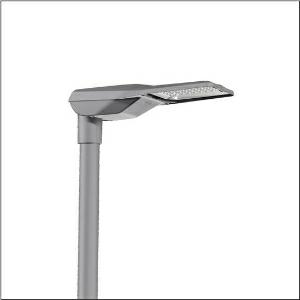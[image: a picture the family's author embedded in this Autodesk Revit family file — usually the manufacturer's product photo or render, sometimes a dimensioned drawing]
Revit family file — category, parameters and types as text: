
# Revit family: streetlight_sl_21_iq_mini___st0_5a_5xe2b41d08gb_120c
name_source: partatom
category: Lighting Fixtures
units: mm (PartAtom-declared; Revit-internal decimal feet)

## family parameters
Cut with Voids When Loaded = No
Host = Face
Light Source = No
Part Type = Normal
Room Calculation Point = No
Round Connector Dimension = Use Diameter
Shared = No

## types (1)
- --- (1 x LED, 5920 lm, 37.1 W, 4000K)
    Apparent Load = 37 VA
    CIE Flux Codes = 41 75 97 100 100
    Color Rendering = 70
    Color Temperature = 4000K
    Default Elevation = 1800 mm
    Description = Streetlight SL 21 iQ mini, mast luminaire, primary light control with lens, of PMMA, primary optical cover: cover, of toughened safety glass, transparent, light distribution: ST0.5a, light emission: direct distribution, primary light characteristic: asymmetric, installation type: post-top, side-entry, LED, High Power LED, rated luminous flux: 5.920lm, luminous efficacy: 160lm/W, light colour: 740, colour temperature: 4000K, control gear: iQ-Comfort, control: Auto-Match, Temp-Guard, Lumen-Switch, Night-Set, Smart-Wire, Light-Fading, Desk-Remote (wireless, voltage-free reading and setting of iQ features in the workshop via application-optimized NFC function/RFID function), optimised constant luminous flux control (CLO 2.0), pre-setting: linear dimming characteristic, mains connection: 220..240V, AC, 50/60Hz, start of lifetime: 37W, end of service life: 39W, reduction: 18W, luminaire housing, of diecast aluminium, powder-coated, SITECO metallic grey (DB 702S), corrosivity category C5 high according to DIN EN ISO 12944, please order mast flange separately, inclination adjustable: 0°, 5°, 10°, 15°, sealing non-destructively replaceable, multi-level sealing system, length: 628mm, width: 235mm, height: 110mm, mast flange for spigot size: 42mm (side-entry): 5XC10008XM4, 60/48mm (side-entry/post-top): 5XC10108XM2, 76/60mm (side-entry/post-top): 5XC10108XM1, mounting height: 4..8m, protection rating (complete): IP66, insulation class (complete): insulation class II (safety insulation), certification: CE, ENEC, ENEC+, VDE, impact resistance: IK10, permissible operating ambient temperature for outdoor applications: -40..+50°C, standard-compliant lighting for roads and squares, packaging unit: 1 piece

Light Distribution: ST0.5a
    Height = 110 mm
    Lamp = 1 x LED
    Lamp Light Flux = 5920 lm
    Lamp Power = 37.1 W
    Lamp count = 1
    Length = 625 mm
    Luminous efficacy = 160 lm/W
    Manufacturer = Siteco
    ModVariant = No
    Model = 5XE2B41D08GB
    Number of Poles = 1
    OnlyDefault = Yes
    Power Factor = 1
    Product Name = Streetlight SL 21 iQ mini | ST0.5a
    Product group = mast luminaire | pylon top
    ProductGroupID = 6100
    Protection Class = Protection class II
    Protection Degree = IP 66
    RLX_Detail_Level = 1
    RLX_Emergency_Light_Flux = 0 lm
    RLX_Emergency_Type = 0
    RLX_Emergency_Type_DB = No
    RlxData = <blob elided: 37341 chars, md5=ed57a155>
    Socket = socket
    Standby Power = 0 W
    System Light Flux = 5920 lm
    System Power = 37 W
    Type Comments = factory setting: luminous flux: 100 % | dim-lin: 254 | 385 mA
    Type Image = l_1003519.jpg
    URL = http://relux.com
    VarID = @adj_188801
    Voltage = 0 V
    Weight = 0.00 kg
    Width = 234 mm

## geometry (parser evidence)
native form markers: Blend x4, Sweep x11
no freeform markers — native parametric forms only
